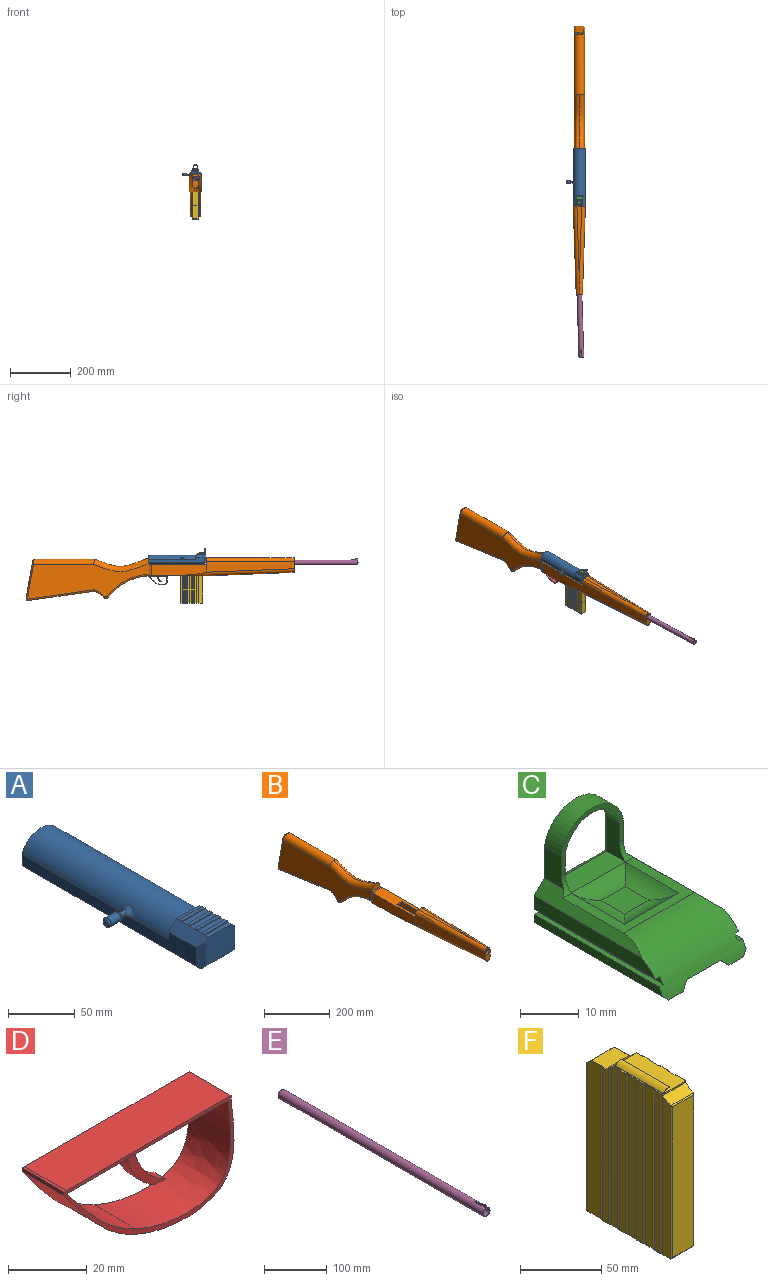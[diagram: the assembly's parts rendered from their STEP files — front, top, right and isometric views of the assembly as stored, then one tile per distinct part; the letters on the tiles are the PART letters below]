
ASSEMBLY  parts=6 mates=5
PART A: 54 faces, bbox 62x188.8x31 mm
  f0: bspline ~4.38x3.72mm, area 6.1mm2, adj f1,f6,f46,f53
  f1: bspline ~6.41x5.39mm, area 13mm2, adj f0,f6,f46,f52
  f2: plane 183.8x5mm, normal (-0.71,0,-0.71), area 1057.8mm2, adj f6,f7,f37,f40,f41,f42,f45
  f3: plane 27.57x24mm, normal (0,0,1), area 450.2mm2, adj f11,f12,f13,f16,f19,f20,f21,f24
  f4: plane 24x3.28mm, normal (0,0,1), area 78.7mm2, adj f9,f12,f13,f14
  f5: plane 183.8x17mm, normal (1,0,0), area 2039.5mm2, adj f8,f9,f10,f12,f36,f39
  f6: plane 183.81x17.01mm, normal (-1,0,0), area 2039.5mm2, adj f0,f1,f2,f8,f9,f10,f13,f34
  f7: plane 178.8x30mm, normal (0,0,-1), area 2723.4mm2, adj f2,f35,f39,f40,f41,f44,f45
  f8: cylinder r=21mm len=155mm, axis (0,1,0), area 8118mm2, adj f5,f6,f9,f10,f52
  f9: plane 40x15mm, normal (0,1,0), area 107.8mm2, adj f4,f5,f6,f8,f12,f13
  f10: plane 40x24.6mm, normal (0,1,0), area 828.2mm2, adj f5,f6,f8,f40
  f11: plane 30x25mm, normal (0,-1,0), area 741mm2, adj f3,f12,f13,f34,f35,f36
  f12: plane 33.8x8mm, normal (0.71,0,0.71), area 364.7mm2, adj f3,f4,f5,f9,f11,f17,f22,f27
  f13: plane 33.8x8mm, normal (-0.71,0,0.71), area 364.7mm2, adj f3,f4,f6,f9,f11,f15,f34
  f14: plane 24x1mm, normal (0,1,0), area 24mm2, adj f4,f15,f17,f18
  f15: plane 2.94x1mm, normal (-1,0,0), area 2.9mm2, adj f13,f14,f16,f18
  f16: plane 24x1mm, normal (0,-1,0), area 24mm2, adj f3,f15,f17,f18
  f17: plane 2.94x1mm, normal (1,0,0), area 2.9mm2, adj f12,f14,f16,f18
  f18: plane 24x2.94mm, normal (0,0,1), area 70.7mm2, adj f14,f15,f16,f17
  f19: plane 23.97x1mm, normal (0,1,0), area 24mm2, adj f3,f20,f22,f23
  f20: plane 2.94x1mm, normal (-1,0,0), area 2.9mm2, adj f3,f19,f21,f23
  f21: plane 23.97x1mm, normal (0,-1,0), area 24mm2, adj f3,f20,f22,f23
  f22: plane 2.94x1mm, normal (1,0,0), area 2.9mm2, adj f12,f19,f21,f23
  f23: plane 23.97x2.94mm, normal (0,0,1), area 70.6mm2, adj f19,f20,f21,f22
  f24: plane 23.94x1mm, normal (0,1,0), area 23.9mm2, adj f3,f25,f27,f28
  f25: plane 2.94x1mm, normal (-1,0,0), area 2.9mm2, adj f3,f24,f26,f28
  f26: plane 23.94x1mm, normal (0,-1,0), area 23.9mm2, adj f3,f25,f27,f28
  f27: plane 2.94x1mm, normal (1,0,0), area 2.9mm2, adj f12,f24,f26,f28
  f28: plane 23.94x2.94mm, normal (0,0,1), area 70.5mm2, adj f24,f25,f26,f27
  f29: plane 23.91x1mm, normal (0,1,0), area 23.9mm2, adj f3,f30,f32,f33
  f30: plane 2.94x1mm, normal (-1,0,0), area 2.9mm2, adj f3,f29,f31,f33
  f31: plane 23.91x1mm, normal (0,-1,0), area 23.9mm2, adj f3,f30,f32,f33
  f32: plane 2.94x1mm, normal (1,0,0), area 2.9mm2, adj f12,f29,f31,f33
  f33: plane 23.91x2.94mm, normal (0,0,1), area 70.4mm2, adj f29,f30,f31,f32
  f34: plane 22x5mm, normal (-0.71,-0.71,0), area 137.9mm2, adj f6,f11,f13,f37
  f35: plane 30x5mm, normal (0,-0.71,-0.71), area 212.1mm2, adj f7,f11,f37,f38
  f36: plane 22x5mm, normal (0.71,-0.71,0), area 137.9mm2, adj f5,f11,f12,f38
  f37: plane 5x5mm, normal (-0.58,-0.58,-0.58), area 21.7mm2, adj f2,f34,f35
  f38: plane 5x5mm, normal (0.58,-0.58,-0.58), area 21.7mm2, adj f35,f36,f39
  f39: plane 183.8x5mm, normal (0.71,0,-0.71), area 1281.9mm2, adj f5,f7,f38,f40
  f40: plane 40x5mm, normal (0,0.71,-0.71), area 247.5mm2, adj f2,f7,f10,f39
  f41: plane 27.73x15mm, normal (0,-1,0), area 414.7mm2, adj f2,f7,f42,f43,f44
  f42: plane 100.94x13.43mm, normal (1,0,0), area 1355.6mm2, adj f2,f41,f43,f45
  f43: plane 100.94x27.73mm, normal (0,0,-1), area 2799mm2, adj f41,f42,f44,f45
  f44: plane 100.94x15mm, normal (-1,0,0), area 1514.2mm2, adj f7,f41,f43,f45
  f45: plane 27.73x15mm, normal (0,1,0), area 414.7mm2, adj f2,f7,f42,f43,f44
  f46: cylinder r=2mm len=7.01mm, axis (-1,0,0), area 50mm2, adj f0,f1,f49,f52,f53
  f47: cylinder r=3.97mm len=10.24mm, axis (1,0,0), area 255.4mm2, adj f50,f51
  f48: plane 3.94x3.94mm, normal (-1,0,0), area 12.2mm2, adj f51
  f49: cone r=7mm half-angle=45deg, axis (-1,0,0), area 33.8mm2, adj f46,f50
  f50: bspline ~7.95x7.94mm, area 37.3mm2, adj f47,f49
  f51: torus R=1.97mm, axis (-1,0,0), area 64mm2, adj f47,f48
  f52: bspline ~14x8.62mm, area 95mm2, adj f1,f8,f46,f53
  f53: bspline ~6.41x5.39mm, area 13mm2, adj f0,f6,f46,f52
PART B: 91 faces, bbox 49.4x890.3x146.1 mm
  f0: plane 82x5mm, normal (-1,0,0), area 397.5mm2, adj f3,f5,f85,f90
  f1: plane 82x5mm, normal (1,0,0), area 397.5mm2, adj f3,f5,f85,f90
  f2: plane 188.4x40mm, normal (0,0,-1), area 5073.2mm2, adj f9,f11,f12,f13,f14,f20,f21,f47
  f3: plane 182.2x40mm, normal (0,0,1), area 5648mm2, adj f0,f1,f6,f9,f11,f45,f73,f85
  f4: plane 188.63x30mm, normal (0,0,1), area 4018mm2, adj f53,f55,f56,f57,f58,f62,f63,f64
  f5: plane 177.2x30mm, normal (0,0,-1), area 3776mm2, adj f0,f1,f52,f53,f54,f55,f73,f75
  f6: plane 40.17x22.14mm, normal (0,1,0), area 308mm2, adj f3,f7,f8,f10,f51,f52,f54,f81
  f7: plane 243.76x15.99mm, normal (0,0,1), area 1948.5mm2, adj f6,f81,f82
  f8: plane 291.21x35.99mm, normal (-1,-0.03,0), area 8826.1mm2, adj f6,f11,f48,f82,f83
  f9: plane 182.2x38.03mm, normal (1,0,0), area 6487.3mm2, adj f2,f3,f10,f20,f45,f84
  f10: plane 290.52x35.97mm, normal (1,-0.03,0), area 8806.7mm2, adj f6,f9,f48,f81,f84
  f11: plane 182.2x38.03mm, normal (-1,0,0), area 6489.7mm2, adj f2,f3,f8,f21,f45,f83
  f12: plane 38.08x5.08mm, normal (0,1,0), area 5.5mm2, adj f2,f18,f20,f34,f46
  f13: plane 38.08x5.08mm, normal (0,1,0), area 5.5mm2, adj f2,f19,f21,f30,f46
  f14: cylinder r=174.95mm len=132.61mm, axis (-1,0,0), area 3866.6mm2, adj f2,f22,f30,f34
  f15: cylinder r=70.7mm len=29.31mm, axis (-1,0,0), area 886.7mm2, adj f16,f22,f28,f32
  f16: plane 220.95x31.05mm, normal (0,-0.14,-0.99), area 5578mm2, adj f15,f26,f27,f31
  f17: plane 122.66x21.63mm, normal (0,0.98,0.17), area 2584.8mm2, adj f38,f39,f40,f41,f42,f43
  f18: plane 402.07x118.28mm, normal (1,0,0), area 29947.3mm2, adj f12,f24,f31,f32,f33,f34,f36,f37
  f19: plane 402.05x118.26mm, normal (-1,0,0), area 29947.3mm2, adj f13,f25,f27,f28,f29,f30,f35,f36
  f20: cylinder r=13.48mm len=38mm, axis (0,0,1), area 271mm2, adj f2,f9,f12,f46
  f21: cylinder r=13.48mm len=38mm, axis (0,0,1), area 271mm2, adj f2,f11,f13,f46
  f22: cylinder r=12mm len=25mm, axis (-1,0,0), area 527.2mm2, adj f14,f15,f29,f33
  f23: plane 16.97x5.84mm, normal (0,0.64,0.77), area 53.1mm2, adj f39,f41,f43
  f24: plane 127.95x26.23mm, normal (0.71,0.7,0.12), area 623mm2, adj f18,f26,f31,f36,f40,f42,f43
  f25: plane 127.95x26.23mm, normal (-0.71,0.7,0.12), area 623mm2, adj f19,f26,f27,f36,f38,f39,f40
  f26: plane 34.23x4.77mm, normal (0,0.72,-0.69), area 172.5mm2, adj f16,f24,f25,f27,f31,f40
  f27: cylinder r=5mm len=224.48mm, axis (0,0.99,-0.14), area 1763.6mm2, adj f16,f19,f25,f26,f28
  f28: torus R=75.7mm, axis (1,0,0), area 290.4mm2, adj f15,f19,f27,f29
  f29: torus R=7mm, axis (1,0,0), area 140.6mm2, adj f19,f22,f28,f30
  f30: torus R=179.95mm, axis (1,0,0), area 1228.1mm2, adj f13,f14,f19,f29
  f31: cylinder r=5mm len=224.48mm, axis (0,-0.99,0.14), area 1763.6mm2, adj f16,f18,f24,f26,f32
  f32: torus R=75.7mm, axis (1,0,0), area 290.4mm2, adj f15,f18,f31,f33
  f33: torus R=7mm, axis (1,0,0), area 140.6mm2, adj f18,f22,f32,f34
  f34: torus R=179.95mm, axis (1,0,0), area 1228.1mm2, adj f12,f14,f18,f33
  f35: bspline ~194.92x47mm, area 5173.8mm2, adj f19,f36,f37,f44
  f36: cylinder r=17.5mm len=201.46mm, axis (0,-1,0), area 10942.9mm2, adj f18,f19,f24,f25,f35,f37,f39,f43
  f37: bspline ~197.39x46.49mm, area 5173.8mm2, adj f18,f35,f36,f44
  f38: cylinder r=5mm len=123.55mm, axis (0,-0.17,0.98), area 482.8mm2, adj f17,f25,f39,f40
  f39: bspline ~17.41x15.77mm, area 88.5mm2, adj f17,f23,f25,f36,f38,f41
  f40: cylinder r=5mm len=29.12mm, axis (1,0,0), area 118.2mm2, adj f17,f24,f25,f26,f38,f42
  f41: cylinder r=5mm len=14.6mm, axis (1,0,0), area 48mm2, adj f17,f23,f39,f43
  f42: cylinder r=5mm len=123.55mm, axis (0,-0.17,0.98), area 482.8mm2, adj f17,f24,f40,f43
  f43: bspline ~17.41x15.77mm, area 88.5mm2, adj f17,f23,f24,f36,f41,f42
  f44: plane 37.95x24.95mm, normal (0,-1,0), area 628.8mm2, adj f18,f19,f35,f37,f46
  f45: plane 40x0.03mm, normal (0,1,0), area 1.1mm2, adj f3,f9,f11,f46
  f46: plane 40x6.59mm, normal (0,0,1), area 251.6mm2, adj f12,f13,f20,f21,f44,f45
  f47: plane 245.15x16.06mm, normal (0,-0.04,-1), area 1968.1mm2, adj f2,f83,f84
  f48: plane 48.85x21.37mm, normal (0.03,-1,0), area 693mm2, adj f8,f10,f49,f81,f82,f83,f84
  f49: cylinder r=8mm len=200.42mm, axis (0.03,-1,0), area 10053.1mm2, adj f48,f50
  f50: plane 16x15.99mm, normal (0.03,-1,0), area 201.1mm2, adj f49
  f51: plane 267.86x29.99mm, normal (0,0,-1), area 3420.9mm2, adj f6,f52,f54,f79,f80
  f52: plane 286.13x49.99mm, normal (1,0.03,0), area 8149.4mm2, adj f5,f6,f51,f55,f73,f77,f78,f79
  f53: plane 181.85x28.03mm, normal (-1,0,0), area 5096.4mm2, adj f4,f5,f54,f64,f75,f76,f77
  f54: plane 285.76x49.95mm, normal (-1,0.03,0), area 10833.1mm2, adj f5,f6,f51,f53,f73,f77,f78,f79
  f55: plane 181.85x28.03mm, normal (1,0,0), area 5096.4mm2, adj f4,f5,f52,f65,f75,f76,f77
  f56: plane 28x2.05mm, normal (0,-1,0), area 57.4mm2, adj f4,f62,f64,f76
  f57: plane 28x2.05mm, normal (0,-1,0), area 57.4mm2, adj f4,f63,f65,f76
  f58: cylinder r=179.95mm len=136.5mm, axis (-1,0,0), area 3979.6mm2, adj f4,f62,f63,f66
  f59: cylinder r=75.7mm len=32.54mm, axis (-1,0,0), area 979.9mm2, adj f60,f62,f63,f66
  f60: plane 219.59x30.86mm, normal (0,0.14,0.99), area 5543.7mm2, adj f59,f62,f63,f69
  f61: plane 126.43x23.92mm, normal (0,-0.98,-0.17), area 2600.7mm2, adj f67,f68,f69,f71
  f62: plane 404.8x115.93mm, normal (-1,0,0), area 29811mm2, adj f4,f56,f58,f59,f60,f66,f67,f69
  f63: plane 404.8x115.91mm, normal (1,0,0), area 29811mm2, adj f4,f57,f58,f59,f60,f66,f68,f69
  f64: cylinder r=8.48mm len=28mm, axis (0,0,1), area 53.8mm2, adj f4,f53,f56,f76
  f65: cylinder r=8.48mm len=28mm, axis (0,0,1), area 53.8mm2, adj f4,f55,f57,f76
  f66: cylinder r=7mm len=25mm, axis (-1,0,0), area 307.5mm2, adj f58,f59,f62,f63
  f67: plane 121.77x23.12mm, normal (-0.71,-0.7,-0.12), area 349.6mm2, adj f61,f62,f69,f71
  f68: plane 121.77x23.12mm, normal (0.71,-0.7,-0.12), area 349.6mm2, adj f61,f63,f69,f71
  f69: plane 25x2.15mm, normal (0,-0.72,0.69), area 69.6mm2, adj f60,f61,f62,f63,f67,f68
  f70: bspline ~188.2x39.69mm, area 3605.2mm2, adj f63,f71,f72,f74
  f71: cylinder r=12.5mm len=199.53mm, axis (0,-1,0), area 7792.9mm2, adj f61,f62,f63,f67,f68,f70,f72
  f72: bspline ~194.87x40.84mm, area 3605.1mm2, adj f62,f70,f71,f74
  f73: plane 29.99x5mm, normal (0,-1,0), area 150mm2, adj f3,f5,f52,f54
  f74: plane 27.11x21.76mm, normal (0,1,0), area 419.1mm2, adj f62,f63,f70,f72,f76
  f75: plane 30x0.03mm, normal (0,-1,0), area 0.8mm2, adj f5,f53,f55,f76
  f76: plane 30x16.59mm, normal (0,0,-1), area 447mm2, adj f53,f55,f56,f57,f62,f63,f64,f65
  f77: plane 287.29x30mm, normal (0,0.04,1), area 5921.8mm2, adj f4,f52,f53,f54,f55,f78
  f78: plane 16.09x11.25mm, normal (-0.03,1,0), area 170.9mm2, adj f52,f54,f77,f79
  f79: cylinder r=13mm len=200.5mm, axis (0.03,-1,0), area 5774.3mm2, adj f51,f52,f54,f78,f80
  f80: plane 24.03x18.53mm, normal (-0.03,1,0), area 387mm2, adj f51,f52,f79
  f81: cylinder r=12mm len=291.6mm, axis (-0.03,-1,0), area 5446mm2, adj f6,f7,f10,f48,f82
  f82: cylinder r=12mm len=291.6mm, axis (-0.03,1,0), area 5451.9mm2, adj f6,f7,f8,f48,f81
  f83: cylinder r=12mm len=389.64mm, axis (0.03,-1,0.04), area 6090.4mm2, adj f2,f8,f11,f47,f48,f84
  f84: cylinder r=12mm len=389.57mm, axis (0.03,1,-0.04), area 6081.3mm2, adj f2,f9,f10,f47,f48,f83
  f85: plane 20x5mm, normal (0,-1,0), area 100mm2, adj f0,f1,f3,f5
  f86: plane 80x5mm, normal (1,0,0), area 400mm2, adj f2,f4,f87,f89
  f87: plane 20x5mm, normal (0,-1,0), area 100mm2, adj f2,f4,f86,f88
  f88: plane 80x5mm, normal (-1,0,0), area 400mm2, adj f2,f4,f87,f89
  f89: plane 20x5mm, normal (0,1,0), area 100mm2, adj f2,f4,f86,f88
  f90: plane 20x5mm, normal (0,0.71,0.71), area 141.4mm2, adj f0,f1,f3,f5
PART C: 42 faces, bbox 20x31.3x23.2 mm
  f0: plane 17x14.57mm, normal (0,0,1), area 80.8mm2, adj f15,f16,f25,f26,f27,f28,f37
  f1: plane 29.16x1mm, normal (0,0,-1), area 29.2mm2, adj f8,f29,f34,f37
  f2: plane 30x1mm, normal (0,0,1), area 30mm2, adj f3,f5,f34,f37
  f3: plane 20x2.63mm, normal (0,1,0), area 38mm2, adj f2,f5,f7,f10,f11,f12,f13,f14
  f4: plane 30x1.12mm, normal (1,0,0), area 32.4mm2, adj f32,f33,f35,f36,f37
  f5: plane 30.91x1.63mm, normal (-1,0,0), area 49.7mm2, adj f2,f3,f31,f37
  f6: plane 29.16x2.75mm, normal (1,0,0), area 76.2mm2, adj f16,f29,f32,f37
  f7: plane 30.91x1.63mm, normal (1,0,0), area 49.7mm2, adj f3,f30,f33,f37
  f8: plane 29.16x2.75mm, normal (-1,0,0), area 76.2mm2, adj f1,f15,f29,f37
  f9: cylinder r=7.61mm len=15mm, axis (0,-1,0), area 85.3mm2, adj f17,f18,f19,f39
  f10: plane 31.31x3.5mm, normal (0,0,-1), area 109.6mm2, adj f3,f12,f31,f37
  f11: plane 31.31x3.5mm, normal (0,0,-1), area 109.6mm2, adj f3,f13,f30,f37
  f12: plane 31.33x1.43mm, normal (0.71,0,-0.71), area 62.1mm2, adj f3,f10,f14,f37
  f13: plane 31.33x1.43mm, normal (-0.71,0,-0.71), area 62.1mm2, adj f3,f11,f14,f37
  f14: plane 30.71x8.17mm, normal (0,0,-1), area 250.9mm2, adj f3,f12,f13,f37
  f15: plane 25.81x2.5mm, normal (-0.71,0,0.71), area 57.8mm2, adj f0,f8,f18,f25,f29,f37,f41
  f16: plane 25.81x2.5mm, normal (0.71,0,0.71), area 57.8mm2, adj f0,f6,f19,f25,f29,f37,f38
  f17: plane 15x10.32mm, normal (0,-1,0), area 27.6mm2, adj f9,f18,f19,f20,f21,f22,f25
  f18: plane 6.5x4.67mm, normal (-1,0,0), area 26.5mm2, adj f9,f15,f17,f25,f39,f41
  f19: plane 6.5x4.67mm, normal (1,0,0), area 26.5mm2, adj f9,f16,f17,f25,f38,f39
  f20: plane 7.29x4.39mm, normal (-1,0,0), area 23.4mm2, adj f17,f21,f23,f25,f38
  f21: cylinder r=6.61mm len=13.03mm, axis (0,-1,0), area 55.6mm2, adj f17,f20,f22,f39
  f22: plane 7.29x4.39mm, normal (1,0,0), area 23.4mm2, adj f17,f21,f23,f25,f41
  f23: plane 13.03x4.39mm, normal (0,0,1), area 57.2mm2, adj f20,f22,f25,f40
  f24: plane 5.86x5.69mm, normal (0,0,1), area 33.4mm2, adj f25,f26,f27,f28
  f25: cylinder r=5mm len=17mm, axis (1,0,0), area 48mm2, adj f0,f15,f16,f17,f18,f19,f20,f22
  f26: cylinder r=5mm len=12.84mm, axis (0,-1,0), area 37.6mm2, adj f0,f24,f25,f28
  f27: cylinder r=5mm len=12.84mm, axis (0,-1,0), area 37.6mm2, adj f0,f24,f25,f28
  f28: cylinder r=5mm len=13mm, axis (1,0,0), area 38.3mm2, adj f0,f24,f26,f27
  f29: plane 20x5.24mm, normal (0,1,0), area 69.3mm2, adj f1,f6,f8,f15,f16,f32,f35,f38
  f30: plane 31.32x1.01mm, normal (0.71,0,-0.71), area 44mm2, adj f3,f7,f11,f37
  f31: plane 31.32x1.01mm, normal (-0.71,0,-0.71), area 44mm2, adj f3,f5,f10,f37
  f32: plane 29.16x1mm, normal (0,0,-1), area 29.2mm2, adj f4,f6,f29,f37
  f33: plane 30x1mm, normal (0,0,1), area 30mm2, adj f3,f4,f7,f37
  f34: plane 30x1.12mm, normal (-1,0,0), area 32.4mm2, adj f1,f2,f35,f36,f37
  f35: cylinder r=1mm len=18mm, axis (1,0,0), area 20.1mm2, adj f4,f29,f34,f36
  f36: cylinder r=1mm len=18mm, axis (-1,0,0), area 20.1mm2, adj f3,f4,f34,f35
  f37: cylinder r=12mm len=20mm, axis (1,0,0), area 264.7mm2, adj f0,f1,f2,f4,f5,f6,f7,f8
  f38: cylinder r=1mm len=8.37mm, axis (0,0,1), area 12mm2, adj f16,f19,f20,f29,f39,f40
  f39: torus R=7.61mm, axis (0,-1,0), area 30.8mm2, adj f9,f18,f19,f21,f38,f41
  f40: cylinder r=1mm len=15.03mm, axis (1,0,0), area 21.6mm2, adj f23,f29,f38,f41
  f41: cylinder r=1mm len=8.37mm, axis (0,0,-1), area 12mm2, adj f15,f18,f22,f29,f39,f40
PART D: 16 faces, bbox 62.1x15x31.1 mm
  f0: cylinder r=19.52mm len=17.98mm, axis (0,1,0), area 87.4mm2, adj f1,f3,f4,f5
  f1: plane 4x3.7mm, normal (0,0,-1), area 14.8mm2, adj f0,f2,f3,f4
  f2: cylinder r=20.36mm len=17.98mm, axis (0,1,0), area 89.7mm2, adj f1,f3,f4,f5
  f3: plane 17.98x14.02mm, normal (0,-1,0), area 54.7mm2, adj f0,f1,f2,f5
  f4: plane 17.98x14.02mm, normal (0,1,0), area 54.7mm2, adj f0,f1,f2,f5
  f5: plane 57.99x15mm, normal (0,0,-1), area 859.6mm2, adj f0,f2,f3,f4,f8,f9,f10,f11
  f6: extruded ~25.85x25mm, area 546.2mm2, adj f7,f10,f11,f12
  f7: extruded ~35.23x28.88mm, area 880.2mm2, adj f6,f10,f11,f13
  f8: extruded ~33.99x27.51mm, area 849mm2, adj f5,f9,f10,f11
  f9: extruded ~24.91x23.3mm, area 517.2mm2, adj f5,f8,f10,f11
  f10: plane 62.12x31.07mm, normal (0,-1,0), area 182.6mm2, adj f5,f6,f7,f8,f9,f12,f13,f14
  f11: plane 62.12x31.07mm, normal (0,1,0), area 182.6mm2, adj f5,f6,f7,f8,f9,f12,f13,f14
  f12: plane 15x1.11mm, normal (-1,0,0), area 16.6mm2, adj f6,f10,f11,f15
  f13: plane 15x1.04mm, normal (1,0,0), area 15.6mm2, adj f7,f10,f11,f14
  f14: plane 59.06x15mm, normal (0,0,1), area 886mm2, adj f10,f11,f13,f15
  f15: plane 15x0.94mm, normal (0.07,0,1), area 14.1mm2, adj f10,f11,f12,f14
PART E: 8 faces, bbox 16x460x21.4 mm
  f0: plane 21.37x16mm, normal (0,-1,0), area 56.6mm2, adj f1,f2,f3,f4,f6
  f1: cylinder r=8mm len=460mm, axis (0,1,0), area 23078mm2, adj f0,f3,f4,f5,f7
  f2: cylinder r=7mm len=460mm, axis (0,1,0), area 20231.9mm2, adj f0,f7
  f3: plane 25x5.42mm, normal (1,0,0), area 67.7mm2, adj f0,f1,f6
  f4: plane 25x5.42mm, normal (-1,0,0), area 67.7mm2, adj f0,f1,f6
  f5: plane 1.76x0.05mm, normal (0,-1,0), area 0.1mm2, adj f1,f6
  f6: plane 25x5.42mm, normal (0,0.21,0.98), area 45.1mm2, adj f0,f3,f4,f5
  f7: plane 16x16mm, normal (0,1,0), area 47.1mm2, adj f1,f2
PART F: 99 faces, bbox 21x75x123.7 mm
  f0: plane 73x21mm, normal (0,0,-1), area 326.2mm2, adj f1,f2,f3,f4,f5,f6,f7,f8
  f1: plane 115.59x12.09mm, normal (-1,0,0), area 1390mm2, adj f0,f9,f16,f39,f79
  f2: plane 121x5.62mm, normal (-1,0,0), area 676.3mm2, adj f0,f10,f37,f40,f86,f88
  f3: plane 121x5.62mm, normal (-1,0,0), area 679.5mm2, adj f0,f35,f38,f88
  f4: plane 121x5.62mm, normal (-1,0,0), area 679.5mm2, adj f0,f33,f36,f88
  f5: plane 115.59x12.09mm, normal (1,0,0), area 1390.1mm2, adj f0,f9,f16,f22,f80
  f6: plane 121x5.62mm, normal (1,0,0), area 676.3mm2, adj f0,f10,f21,f24,f86,f88
  f7: plane 121x5.62mm, normal (1,0,0), area 679.6mm2, adj f0,f23,f26,f88
  f8: plane 121x5.62mm, normal (1,0,0), area 679.6mm2, adj f0,f25,f28,f88
  f9: plane 21x13.12mm, normal (0,0,1), area 265.9mm2, adj f1,f5,f10,f16,f20,f22,f32,f39
  f10: plane 21x6.32mm, normal (0,0.57,0.82), area 157.6mm2, adj f2,f6,f9,f20,f21,f32,f40,f86
  f11: cylinder r=23.27mm len=20.01mm, axis (-1,0,0), area 164.7mm2, adj f14,f15,f27,f34,f83,f84,f85,f87
  f12: plane 113.89x18mm, normal (0,-1,0), area 2050mm2, adj f82,f83,f84,f85
  f13: plane 109.18x18mm, normal (0,1,0), area 1965.2mm2, adj f78,f79,f80,f81
  f14: plane 119.85x6.52mm, normal (1,0,0), area 767.4mm2, adj f0,f11,f27,f83
  f15: plane 119.85x6.52mm, normal (-1,0,0), area 767.4mm2, adj f0,f11,f34,f84
  f16: plane 20x4.71mm, normal (0,0.71,0.71), area 133mm2, adj f1,f5,f9,f79,f80,f81
  f17: plane 121x5.02mm, normal (1,0,0), area 608mm2, adj f0,f27,f28,f88
  f18: plane 121x5.02mm, normal (1,0,0), area 608mm2, adj f0,f25,f26,f88
  f19: plane 121x5.02mm, normal (1,0,0), area 608mm2, adj f0,f23,f24,f88
  f20: plane 117.11x5.02mm, normal (1,0,0), area 582.5mm2, adj f0,f9,f10,f21,f22
  f21: cylinder r=5mm len=118.63mm, axis (0,0,-1), area 265.8mm2, adj f0,f6,f10,f20
  f22: cylinder r=5mm len=115.59mm, axis (0,0,-1), area 260.7mm2, adj f0,f5,f9,f20
  f23: cylinder r=5mm len=121mm, axis (0,0,-1), area 272.9mm2, adj f0,f7,f19,f88
  f24: cylinder r=5mm len=121mm, axis (0,0,-1), area 272.9mm2, adj f0,f6,f19,f88
  f25: cylinder r=5mm len=121mm, axis (0,0,-1), area 272.9mm2, adj f0,f8,f18,f88
  f26: cylinder r=5mm len=121mm, axis (0,0,-1), area 272.9mm2, adj f0,f7,f18,f88
  f27: cylinder r=5mm len=121mm, axis (0,0,-1), area 272.7mm2, adj f0,f11,f14,f17,f87,f88
  f28: cylinder r=5mm len=121mm, axis (0,0,-1), area 272.9mm2, adj f0,f8,f17,f88
  f29: plane 121x5.03mm, normal (-1,0,0), area 608mm2, adj f0,f33,f34,f88
  f30: plane 121x5.03mm, normal (-1,0,0), area 608mm2, adj f0,f35,f36,f88
  f31: plane 121x5.03mm, normal (-1,0,0), area 608mm2, adj f0,f37,f38,f88
  f32: plane 117.11x5.03mm, normal (-1,0,0), area 582.5mm2, adj f0,f9,f10,f39,f40
  f33: cylinder r=5mm len=121mm, axis (0,0,-1), area 272.9mm2, adj f0,f4,f29,f88
  f34: cylinder r=5mm len=121mm, axis (0,0,-1), area 272.7mm2, adj f0,f11,f15,f29,f87,f88
  f35: cylinder r=5mm len=121mm, axis (0,0,-1), area 272.9mm2, adj f0,f3,f30,f88
  f36: cylinder r=5mm len=121mm, axis (0,0,-1), area 272.9mm2, adj f0,f4,f30,f88
  f37: cylinder r=5mm len=121mm, axis (0,0,-1), area 272.9mm2, adj f0,f2,f31,f88
  f38: cylinder r=5mm len=121mm, axis (0,0,-1), area 272.9mm2, adj f0,f3,f31,f88
  f39: cylinder r=5mm len=115.59mm, axis (0,0,-1), area 260.7mm2, adj f0,f1,f9,f32
  f40: cylinder r=5mm len=118.63mm, axis (0,0,-1), area 265.8mm2, adj f0,f2,f10,f32
  f41: plane 11.09x0.5mm, normal (1,0,0), area 5.5mm2, adj f0,f42,f76,f77
  f42: plane 16x0.5mm, normal (0,-1,0), area 8mm2, adj f0,f41,f43,f77
  f43: plane 11.09x0.5mm, normal (-1,0,0), area 5.5mm2, adj f0,f42,f44,f77
  f44: cylinder r=7mm len=2.6mm, axis (0,0,-1), area 1.3mm2, adj f0,f43,f45,f77
  f45: plane 4.19x0.5mm, normal (-1,0,0), area 2.1mm2, adj f0,f44,f46,f77
  f46: cylinder r=7mm len=2.6mm, axis (0,0,-1), area 1.3mm2, adj f0,f45,f47,f77
  f47: plane 5.62x0.5mm, normal (-1,0,0), area 2.8mm2, adj f0,f46,f48,f77
  f48: cylinder r=7mm len=2.6mm, axis (0,0,-1), area 1.3mm2, adj f0,f47,f49,f77
  f49: plane 4.19x0.5mm, normal (-1,0,0), area 2.1mm2, adj f0,f48,f50,f77
  f50: cylinder r=7mm len=2.6mm, axis (0,0,-1), area 1.3mm2, adj f0,f49,f51,f77
  f51: plane 5.62x0.5mm, normal (-1,0,0), area 2.8mm2, adj f0,f50,f52,f77
  f52: cylinder r=7mm len=2.6mm, axis (0,0,-1), area 1.3mm2, adj f0,f51,f53,f77
  f53: plane 4.19x0.5mm, normal (-1,0,0), area 2.1mm2, adj f0,f52,f54,f77
  f54: cylinder r=7mm len=2.6mm, axis (0,0,-1), area 1.3mm2, adj f0,f53,f55,f77
  f55: plane 5.62x0.5mm, normal (-1,0,0), area 2.8mm2, adj f0,f54,f56,f77
  f56: cylinder r=7mm len=2.6mm, axis (0,0,-1), area 1.3mm2, adj f0,f55,f57,f77
  f57: plane 4.19x0.5mm, normal (-1,0,0), area 2.1mm2, adj f0,f56,f58,f77
  f58: cylinder r=7mm len=2.6mm, axis (0,0,-1), area 1.3mm2, adj f0,f57,f59,f77
  f59: plane 5.52x0.5mm, normal (-1,0,0), area 2.8mm2, adj f0,f58,f60,f77
  f60: plane 16x0.5mm, normal (0,1,0), area 8mm2, adj f0,f59,f61,f77
  f61: plane 5.52x0.5mm, normal (1,0,0), area 2.8mm2, adj f0,f60,f62,f77
  f62: cylinder r=7mm len=2.6mm, axis (0,0,-1), area 1.3mm2, adj f0,f61,f63,f77
  f63: plane 4.19x0.5mm, normal (1,0,0), area 2.1mm2, adj f0,f62,f64,f77
  f64: cylinder r=7mm len=2.6mm, axis (0,0,-1), area 1.3mm2, adj f0,f63,f65,f77
  f65: plane 5.62x0.5mm, normal (1,0,0), area 2.8mm2, adj f0,f64,f66,f77
  f66: cylinder r=7mm len=2.6mm, axis (0,0,-1), area 1.3mm2, adj f0,f65,f67,f77
  f67: plane 4.19x0.5mm, normal (1,0,0), area 2.1mm2, adj f0,f66,f68,f77
  f68: cylinder r=7mm len=2.6mm, axis (0,0,-1), area 1.3mm2, adj f0,f67,f69,f77
  f69: plane 5.62x0.5mm, normal (1,0,0), area 2.8mm2, adj f0,f68,f70,f77
  f70: cylinder r=7mm len=2.6mm, axis (0,0,-1), area 1.3mm2, adj f0,f69,f71,f77
  f71: plane 4.19x0.5mm, normal (1,0,0), area 2.1mm2, adj f0,f70,f72,f77
  f72: cylinder r=7mm len=2.6mm, axis (0,0,-1), area 1.3mm2, adj f0,f71,f73,f77
  f73: plane 5.62x0.5mm, normal (1,0,0), area 2.8mm2, adj f0,f72,f74,f77
  f74: cylinder r=7mm len=2.6mm, axis (0,0,-1), area 1.3mm2, adj f0,f73,f75,f77
  f75: plane 4.19x0.5mm, normal (1,0,0), area 2.1mm2, adj f0,f74,f76,f77
  f76: cylinder r=7mm len=2.6mm, axis (0,0,-1), area 1.3mm2, adj f0,f41,f75,f77
  f77: plane 71x17mm, normal (0,0,-1), area 1159.6mm2, adj f41,f42,f43,f44,f45,f46,f47,f48
  f78: cylinder r=1mm len=20mm, axis (1,0,0), area 30.3mm2, adj f0,f13,f79,f80
  f79: cylinder r=1mm len=111.59mm, axis (0,0,1), area 173.6mm2, adj f1,f13,f16,f78,f81
  f80: cylinder r=1mm len=111.59mm, axis (0,0,-1), area 173.6mm2, adj f5,f13,f16,f78,f81
  f81: cylinder r=1mm len=19.41mm, axis (-1,0,0), area 14.7mm2, adj f13,f16,f79,f80
  f82: cylinder r=1mm len=20mm, axis (-1,0,0), area 30.3mm2, adj f0,f12,f83,f84
  f83: cylinder r=1mm len=115.96mm, axis (0,0,1), area 180.9mm2, adj f11,f12,f14,f82,f85
  f84: cylinder r=1mm len=115.96mm, axis (0,0,-1), area 180.9mm2, adj f11,f12,f15,f82,f85
  f85: cylinder r=1mm len=19.87mm, axis (-1,0,0), area 23.1mm2, adj f11,f12,f83,f84
  f86: plane 20x1mm, normal (0,1,0), area 20mm2, adj f2,f6,f10,f88
  f87: plane 20.01x3.72mm, normal (0,-1,0), area 21.3mm2, adj f11,f27,f34,f88,f89,f90,f91
  f88: plane 42.86x21mm, normal (0,0,1), area 865.4mm2, adj f2,f3,f4,f6,f7,f8,f17,f18
  f89: plane 42x0.24mm, normal (1,0,0.01), area 10.1mm2, adj f87,f90,f91,f92
  f90: cylinder r=6.56mm len=42mm, axis (0,-1,0), area 254.2mm2, adj f87,f88,f89,f92
  f91: cylinder r=6.16mm len=42mm, axis (0,-1,0), area 239.2mm2, adj f87,f88,f89,f92
  f92: plane 5.17x2.72mm, normal (0,1,0), area 1.3mm2, adj f88,f89,f90,f91
  f93: plane 73x44mm, normal (1,0,0), area 3212mm2, adj f94,f96,f97,f98
  f94: plane 44x18mm, normal (0,-1,0), area 792mm2, adj f93,f95,f97,f98
  f95: plane 73x44mm, normal (-1,0,0), area 3212mm2, adj f94,f96,f97,f98
  f96: plane 44x18mm, normal (0,1,0), area 792mm2, adj f93,f95,f97,f98
  f97: plane 73x18mm, normal (0,0,-1), area 1314mm2, adj f93,f94,f95,f96
  f98: plane 73x18mm, normal (0,0,1), area 1314mm2, adj f93,f94,f95,f96
PLACE A t=(-128.63,-665.17,-129.34)mm
PLACE B t=(-148.63,-321.2,-265.3)mm fixed
PLACE C rot(axis=(0,0,-1),180deg) t=(-138.63,-754.16,-110.76)mm
PLACE D rot(axis=(0,0,-1),90deg) t=(-141.13,-611.49,-183.38)mm
PLACE E rot(axis=(0,0,1),1.9deg) t=(-161.34,-676.44,-138.37)mm
PLACE F rot(axis=(0,0,-1),180deg) t=(-138.63,-726.27,-235.02)mm
MATE slider F.f77 <-> B.f2  axis (0,0,-1) through (-148.63,-726.58,-272.34)mm
MATE fastened A.f7 <-> B.f46  axis (0,0,-1) through (-148.63,-590.17,-144.34)mm
MATE fastened C.f14 <-> A.f18  axis (0,0,-1) through (-148.63,-743.45,-113.34)mm
MATE fastened D.f14 <-> B.f2  axis (0,0,1) through (-148.63,-586.58,-182.34)mm
MATE fastened E.f1 <-> B.f49  axis (-0.03,1,0) through (-156.75,-816.37,-138.37)mm
